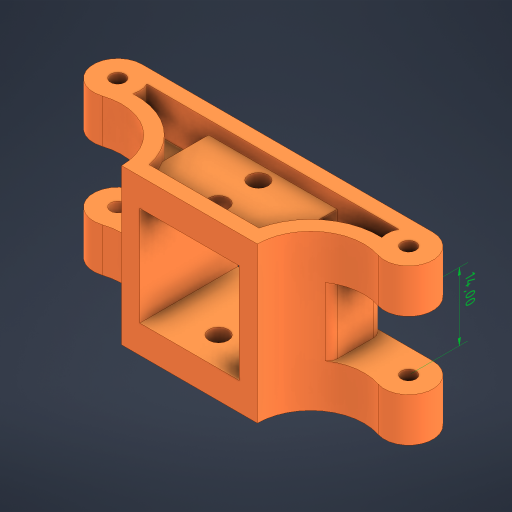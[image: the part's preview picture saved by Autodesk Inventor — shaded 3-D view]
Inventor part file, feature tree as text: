
AUTODESK INVENTOR PART (.ipt)
format: ipt  version: 2024 (Build 280153000, 153)  size: 376,832 bytes
history: native  units: mm
features: other x17, extrude x4, sketch x4, mirror x1, shell x1, fillet x1
ambient origin geometry x8: Origin, YZ Plane, XZ Plane, XY Plane, X Axis, Y Axis, Z Axis, Center Point
bodies: Body1 (feature_tree)
feature tree (28):
  other  "Твердое тело1"
  other  "Аннотации"
  extrude  "Выдавливание1"  Depth=3.0mm
  extrude  "Выдавливание2"  Depth=28.0mm
  other  "РабПлоскость2"
  extrude  "Выдавливание4"  Depth=11.0mm
  mirror  "Зеркальное отражение1"
  other  "Непосредственное редактирование2"
  shell  "Оболочка3"  Thickness=5.0mm
  extrude  "Выдавливание5"  Depth=60.0mm
  fillet  "Сопряжение1"  Radius=28.0mm
  other  "Непосредственное редактирование3"
  other  "Непосредственное редактирование4"
  other  "Непосредственное редактирование5"
  sketch  "Эскиз1"
  sketch  "Эскиз2"
  other  "РабПлоскость1"
  sketch  "Эскиз4"
  sketch  "Эскиз5"
  other  "Перенос3"
  other  "Перенос4"
  other  "Перенос5"
  other  "Перенос6"
  other  "Перенос7"
  other  "Перенос8"
  other  "Перенос9"
  other  "Перенос10"
  other  "Линейный размер 1"
